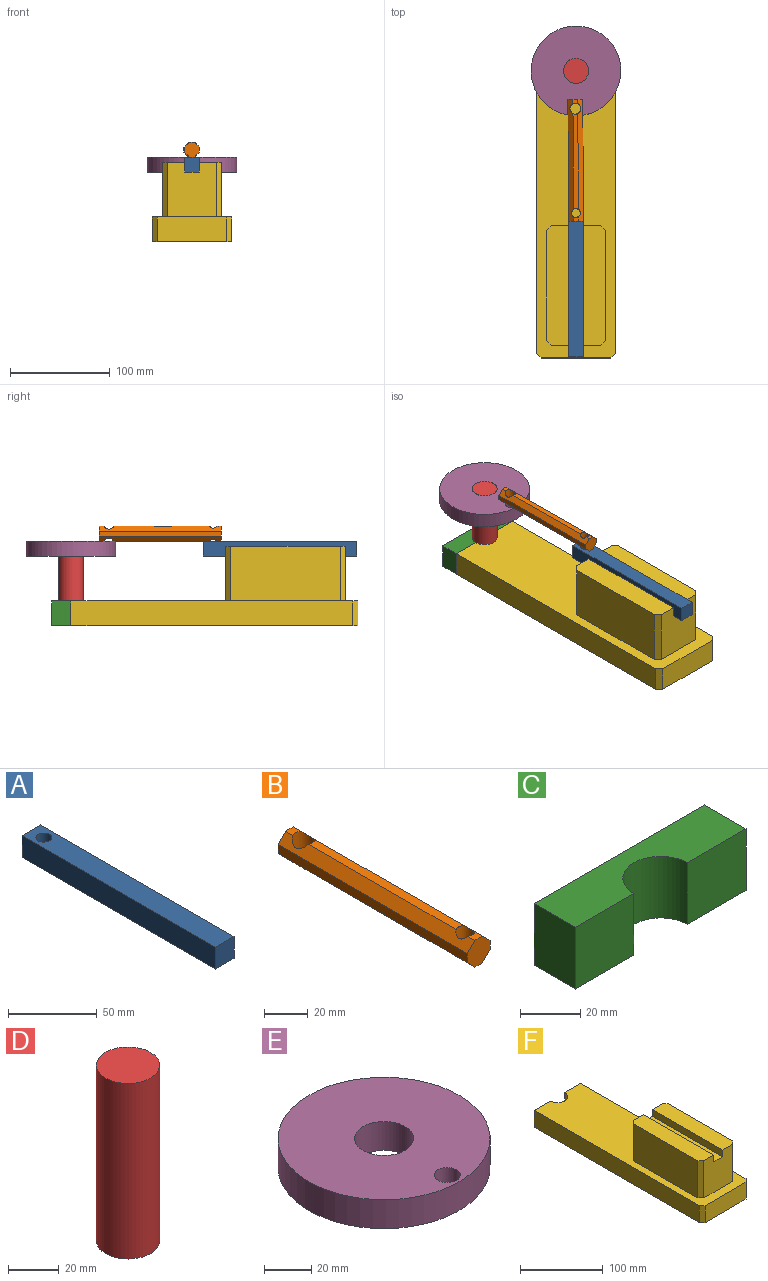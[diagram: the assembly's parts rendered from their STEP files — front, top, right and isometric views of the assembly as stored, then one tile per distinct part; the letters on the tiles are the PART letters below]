
ASSEMBLY  parts=6 mates=6
PART A: 7 faces, bbox 14.9x154.3x15 mm
  f0: plane 15x14.86mm, normal (0,1,0), area 222.8mm2, adj f1,f3,f5,f6
  f1: plane 154.29x15mm, normal (-1,0,0), area 2314.4mm2, adj f0,f2,f5,f6
  f2: plane 15x14.86mm, normal (0,-1,0), area 222.8mm2, adj f1,f3,f5,f6
  f3: plane 154.29x15mm, normal (1,0,0), area 2314.4mm2, adj f0,f2,f5,f6
  f4: cylinder r=4.46mm len=15mm, axis (0,0,1), area 420mm2, adj f5,f6
  f5: plane 154.29x14.86mm, normal (0,0,-1), area 2229.9mm2, adj f0,f1,f2,f3,f4
  f6: plane 154.29x14.86mm, normal (0,0,1), area 2229.9mm2, adj f0,f1,f2,f3,f4
PART B: 16 faces, bbox 14.9x122.6x15 mm
  f0: plane 4.86x4.7mm, normal (0,0,1), area 21mm2, adj f5,f9,f14,f15
  f1: plane 95.99x4.86mm, normal (0,0,1), area 461.9mm2, adj f7,f9,f14,f15
  f2: plane 4.86x4.61mm, normal (0,0,-1), area 20mm2, adj f7,f8,f12,f13
  f3: plane 95.99x4.86mm, normal (0,0,-1), area 461.9mm2, adj f7,f9,f12,f13
  f4: plane 122.64x5mm, normal (1,0,0), area 613.2mm2, adj f5,f8,f13,f15
  f5: plane 15x14.86mm, normal (0,1,0), area 172.8mm2, adj f0,f4,f6,f11,f12,f13,f14,f15
  f6: plane 122.64x5mm, normal (-1,0,0), area 613.2mm2, adj f5,f8,f12,f14
  f7: cylinder r=4.46mm len=15mm, axis (0,0,-1), area 372.9mm2, adj f1,f2,f3,f10,f12,f13,f14,f15
  f8: plane 15x14.86mm, normal (0,-1,0), area 172.8mm2, adj f2,f4,f6,f10,f12,f13,f14,f15
  f9: cylinder r=5.5mm len=15mm, axis (0,0,-1), area 420.2mm2, adj f0,f1,f3,f11,f12,f13,f14,f15
  f10: plane 4.86x4.61mm, normal (0,0,1), area 20mm2, adj f7,f8,f14,f15
  f11: plane 4.86x4.7mm, normal (0,0,-1), area 21mm2, adj f5,f9,f12,f13
  f12: plane 122.64x5mm, normal (-0.71,0,-0.71), area 821.4mm2, adj f2,f3,f5,f6,f7,f8,f9,f11
  f13: plane 122.64x5mm, normal (0.71,0,-0.71), area 821.4mm2, adj f2,f3,f4,f5,f7,f8,f9,f11
  f14: plane 122.64x5mm, normal (-0.71,0,0.71), area 821.4mm2, adj f0,f1,f5,f6,f7,f8,f9,f10
  f15: plane 122.64x5mm, normal (0.71,0,0.71), area 821.4mm2, adj f0,f1,f4,f5,f7,f8,f9,f10
PART C: 8 faces, bbox 80x19.3x25 mm
  f0: plane 25x19.34mm, normal (-1,0,0), area 483.5mm2, adj f1,f5,f6,f7
  f1: plane 27.5x25mm, normal (0,-1,0), area 687.5mm2, adj f0,f2,f6,f7
  f2: cylinder r=12.5mm len=25mm, axis (0,0,1), area 981.7mm2, adj f1,f3,f6,f7
  f3: plane 27.5x25mm, normal (0,-1,0), area 687.5mm2, adj f2,f4,f6,f7
  f4: plane 25x19.34mm, normal (1,0,0), area 483.5mm2, adj f3,f5,f6,f7
  f5: plane 80x25mm, normal (0,1,0), area 2000mm2, adj f0,f4,f6,f7
  f6: plane 80x19.34mm, normal (0,0,-1), area 1301.7mm2, adj f0,f1,f2,f3,f4,f5
  f7: plane 80x19.34mm, normal (0,0,1), area 1301.7mm2, adj f0,f1,f2,f3,f4,f5
PART D: 3 faces, bbox 25x25x85 mm
  f0: cylinder r=12.5mm len=85mm, axis (0,0,-1), area 6675.9mm2, adj f1,f2
  f1: plane 25x25mm, normal (0,0,1), area 490.9mm2, adj f0
  f2: plane 25x25mm, normal (0,0,-1), area 490.9mm2, adj f0
PART E: 5 faces, bbox 90x90x15 mm
  f0: cylinder r=5.5mm len=15mm, axis (0,0,1), area 518.4mm2, adj f3,f4
  f1: cylinder r=12.5mm len=25mm, axis (0,0,1), area 1178.1mm2, adj f3,f4
  f2: cylinder r=45mm len=90mm, axis (0,0,1), area 4241.2mm2, adj f3,f4
  f3: plane 90x90mm, normal (0,0,-1), area 5775.8mm2, adj f0,f1,f2
  f4: plane 90x90mm, normal (0,0,1), area 5775.8mm2, adj f0,f1,f2
PART F: 23 faces, bbox 80x287.8x80 mm
  f0: plane 120x22.17mm, normal (0,0,1), area 2635.4mm2, adj f2,f12,f13,f14,f17,f19
  f1: plane 120x22.17mm, normal (0,0,1), area 2635.4mm2, adj f2,f11,f12,f15,f18,f20
  f2: plane 55x49.2mm, normal (0,-1,0), area 2557.3mm2, adj f0,f1,f3,f14,f15,f16,f19,f20
  f3: plane 287.78x80mm, normal (0,0,1), area 15698.6mm2, adj f2,f4,f5,f6,f7,f8,f9,f11
  f4: plane 282.78x25mm, normal (1,0,0), area 7069.6mm2, adj f3,f5,f10,f22
  f5: plane 27.5x25mm, normal (0,1,0), area 687.5mm2, adj f3,f4,f6,f10
  f6: cylinder r=12.5mm len=25mm, axis (0,0,1), area 981.7mm2, adj f3,f5,f7,f10
  f7: plane 27.5x25mm, normal (0,1,0), area 687.5mm2, adj f3,f6,f8,f10
  f8: plane 282.78x25mm, normal (-1,0,0), area 7069.6mm2, adj f3,f7,f10,f21
  f9: plane 70x25mm, normal (0,-1,0), area 1750mm2, adj f3,f10,f21,f22
  f10: plane 287.78x80mm, normal (0,0,-1), area 22752.2mm2, adj f4,f5,f6,f7,f8,f9,f21,f22
  f11: plane 110x55mm, normal (1,0,0), area 6050mm2, adj f1,f3,f18,f20
  f12: plane 55x49.2mm, normal (0,1,0), area 2557.3mm2, adj f0,f1,f3,f14,f15,f16,f17,f18
  f13: plane 110x55mm, normal (-1,0,0), area 6050mm2, adj f0,f3,f17,f19
  f14: plane 120x10mm, normal (1,0,0), area 1200mm2, adj f0,f2,f12,f16
  f15: plane 120x10mm, normal (-1,0,0), area 1200mm2, adj f1,f2,f12,f16
  f16: plane 120x14.86mm, normal (0,0,1), area 1782.8mm2, adj f2,f12,f14,f15
  f17: plane 55x5mm, normal (-0.71,0.71,0), area 388.9mm2, adj f0,f3,f12,f13
  f18: plane 55x5mm, normal (0.71,0.71,0), area 388.9mm2, adj f1,f3,f11,f12
  f19: plane 55x5mm, normal (-0.71,-0.71,0), area 388.9mm2, adj f0,f2,f3,f13
  f20: plane 55x5mm, normal (0.71,-0.71,0), area 388.9mm2, adj f1,f2,f3,f11
  f21: plane 25x5mm, normal (-0.71,-0.71,0), area 176.8mm2, adj f3,f8,f9,f10
  f22: plane 25x5mm, normal (0.71,-0.71,0), area 176.8mm2, adj f3,f4,f9,f10
PLACE A t=(-93.31,48.66,-52.31)mm
PLACE B rot(axis=(0,0,1),0.3deg) t=(-94.02,48.66,-52.31)mm
PLACE C t=(-93.31,48.66,-52.31)mm
PLACE D t=(-93.31,48.66,-52.31)mm
PLACE E rot(axis=(0,0,-1),0.9deg) t=(-93.6,48.66,-52.31)mm
PLACE F t=(-93.31,48.66,-52.31)mm fixed
MATE revolute B.f7 <-> A.f4  axis (0,0,-1) through (-93.31,-75.51,7.69)mm
MATE revolute E.f1 <-> D.f0  axis (0,0,1) through (-93.31,67.08,7.69)mm
MATE fastened C.f3 <-> F.f5  axis (0,-1,0) through (-67.06,67.08,-64.81)mm
MATE revolute B.f9 <-> E.f0  axis (0,0,-1) through (-93.91,29.15,7.69)mm
MATE slider F.f12 <-> A.f0  axis (0,1,0) through (-100.74,-88.07,-7.31)mm
MATE revolute D.f0 <-> C.f2  axis (0,0,-1) through (-93.31,67.08,-77.31)mm
